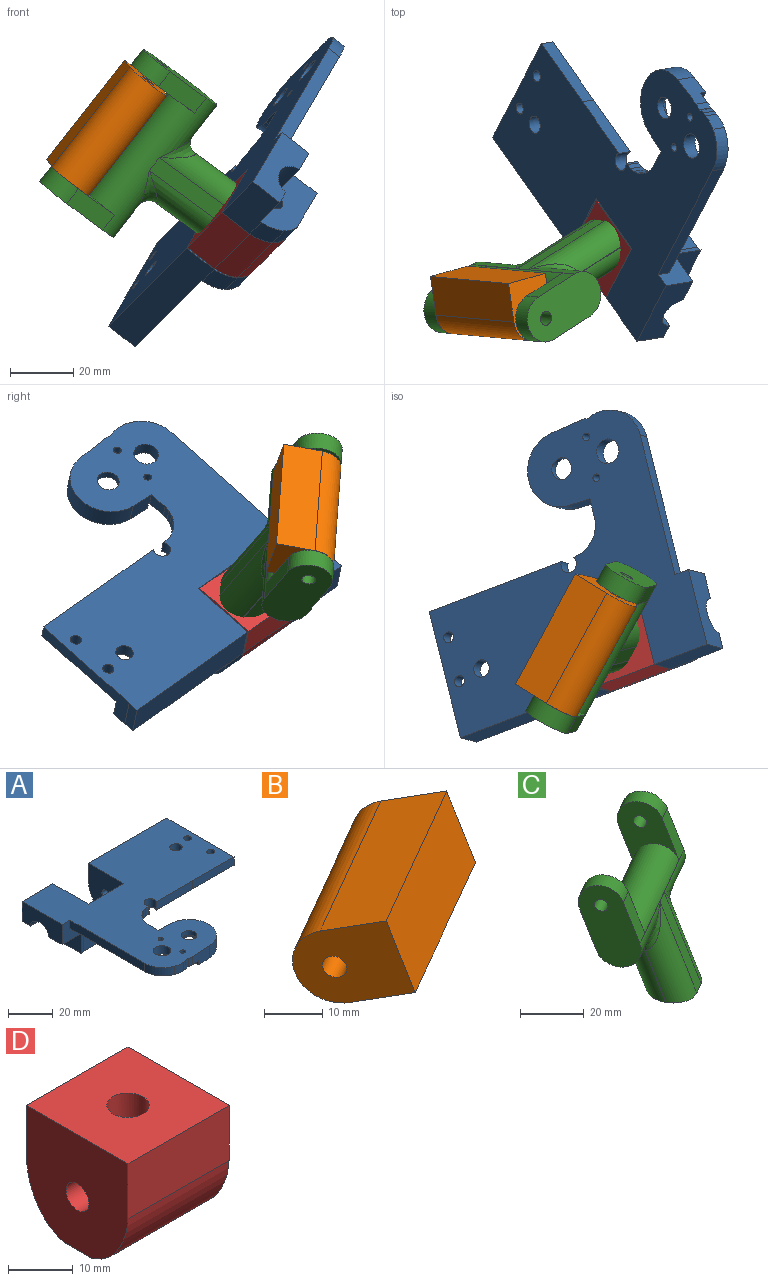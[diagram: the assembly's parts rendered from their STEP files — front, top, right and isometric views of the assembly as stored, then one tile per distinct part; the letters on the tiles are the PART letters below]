
ASSEMBLY  parts=4 mates=2
PART A: 74 faces, bbox 91.3x84.2x21.9 mm
  f0: plane 25.22x10.8mm, normal (-1,0,0), area 227.8mm2, adj f1,f2,f5,f21,f43,f72
  f1: plane 12.09x8.3mm, normal (0,0,-1), area 100.4mm2, adj f0,f7,f21,f72
  f2: plane 91.18x84.09mm, normal (0,0,1), area 4447.4mm2, adj f0,f30,f31,f32,f34,f35,f40,f41
  f3: cylinder r=2.5mm len=7.4mm, axis (1,0,0), area 116.2mm2, adj f8,f40
  f4: cylinder r=2.5mm len=7.4mm, axis (1,0,0), area 116.2mm2, adj f7,f42
  f5: plane 12.09x5.08mm, normal (0,0,-1), area 61.5mm2, adj f0,f7,f21,f43
  f6: plane 41.89x24.6mm, normal (0,0,-1), area 640.6mm2, adj f8,f9,f10,f11,f12,f13,f15,f24
  f7: plane 25.22x16mm, normal (-1,0,0), area 278.4mm2, adj f1,f4,f5,f14,f16,f19,f20,f21
  f8: plane 24.6x14mm, normal (1,0,0), area 244.2mm2, adj f3,f6,f13,f16,f17,f18,f29,f62
  f9: plane 10.48x6.3mm, normal (0,-1,0), area 66mm2, adj f6,f10,f15,f22
  f10: cylinder r=1.92mm len=6.3mm, axis (0,0,-1), area 12.4mm2, adj f6,f9,f11,f22
  f11: plane 10.52x6.64mm, normal (0.85,-0.53,0), area 78.4mm2, adj f6,f10,f12,f22
  f12: cylinder r=9.77mm len=8.3mm, axis (0,0,-1), area 62.3mm2, adj f6,f11,f13,f22
  f13: plane 47.39x17.3mm, normal (0,-1,0), area 687.6mm2, adj f6,f8,f12,f14,f16,f22
  f14: cylinder r=11.65mm len=17.3mm, axis (0,0,-1), area 33.5mm2, adj f7,f13,f16,f22,f72
  f15: plane 6.3x2.78mm, normal (0,-1,0), area 17.5mm2, adj f6,f9,f22,f61
  f16: plane 37.2x17.31mm, normal (0,0,-1), area 301.2mm2, adj f7,f8,f13,f14,f17,f20,f40,f41
  f17: cylinder r=10.47mm len=7.4mm, axis (-1,0,0), area 41.3mm2, adj f8,f16,f18,f40
  f18: cylinder r=13.47mm len=7.71mm, axis (-1,0,0), area 63mm2, adj f8,f17,f40,f62
  f19: cylinder r=13.47mm len=7.71mm, axis (-1,0,0), area 63mm2, adj f7,f20,f42,f43
  f20: cylinder r=10.47mm len=7.4mm, axis (-1,0,0), area 41.3mm2, adj f7,f16,f19,f42
  f21: cylinder r=6mm len=12.09mm, axis (-1,0,0), area 203.6mm2, adj f0,f1,f5,f7
  f22: plane 86.18x75.47mm, normal (0,0,-1), area 2643.1mm2, adj f9,f10,f11,f12,f13,f14,f15,f30
  f23: plane 8.77x4.2mm, normal (0,0.5,-0.87), area 41.3mm2, adj f24,f26,f28,f29
  f24: plane 8.78x1.57mm, normal (0,1,0), area 11.9mm2, adj f6,f23,f28,f29
  f25: plane 8.77x1.57mm, normal (0,-1,0), area 11.9mm2, adj f6,f26,f28,f29
  f26: plane 8.77x4.21mm, normal (0,-0.5,-0.87), area 41.3mm2, adj f23,f25,f28,f29
  f27: plane 7.75x3mm, normal (-1,0,0), area 17.2mm2, adj f6,f28
  f28: cone r=4mm half-angle=60deg, axis (-1,0,0), area 5.8mm2, adj f6,f23,f24,f25,f26,f27
  f29: cone r=4mm half-angle=60deg, axis (1,0,0), area 5.8mm2, adj f6,f8,f23,f24,f25,f26
  f30: plane 7.82x6.7mm, normal (0.05,1,0), area 51.4mm2, adj f2,f22,f34,f37,f39,f47
  f31: cylinder r=5.75mm len=4.5mm, axis (0,0,1), area 9.8mm2, adj f2,f22,f32,f46
  f32: plane 11.46x6.7mm, normal (0.05,-1,0), area 67.4mm2, adj f2,f22,f31,f34,f38,f39
  f33: cylinder r=8.15mm len=16.3mm, axis (0,0,1), area 191.9mm2, adj f22,f36,f37,f38,f39
  f34: cylinder r=12.15mm len=24.26mm, axis (0,0,1), area 246mm2, adj f2,f30,f32,f39
  f35: cylinder r=3.5mm len=7mm, axis (0,0,-1), area 55mm2, adj f2,f36
  f36: plane 16.3x16.3mm, normal (0,0,-1), area 170.2mm2, adj f33,f35
  f37: plane 7.61x2.2mm, normal (-1,0,0), area 16.8mm2, adj f22,f30,f33,f39
  f38: plane 7.62x2.2mm, normal (-1,0,0), area 16.8mm2, adj f22,f32,f33,f39
  f39: plane 25.04x18.66mm, normal (0,0,-1), area 194.9mm2, adj f30,f32,f33,f34,f37,f38
  f40: plane 22.2x21.8mm, normal (-1,0,0), area 440.3mm2, adj f2,f3,f16,f17,f18,f41,f62
  f41: plane 22.4x21.8mm, normal (0,1,0), area 488.3mm2, adj f2,f16,f40,f42
  f42: plane 22.2x21.8mm, normal (1,0,0), area 440.3mm2, adj f2,f4,f16,f19,f20,f41,f43
  f43: plane 19.49x11.13mm, normal (0,1,0), area 212.9mm2, adj f0,f2,f5,f7,f19,f42
  f44: plane 4.5x1.47mm, normal (0.1,-1,0), area 6.6mm2, adj f2,f22,f45,f69
  f45: plane 4.5x1.73mm, normal (0.27,-0.96,0), area 8.1mm2, adj f2,f22,f44,f46
  f46: plane 4.5x0.31mm, normal (0.44,-0.9,0), area 1.6mm2, adj f2,f22,f31,f45
  f47: plane 6.19x4.5mm, normal (1,0,0), area 27.9mm2, adj f2,f22,f30,f48
  f48: plane 4.5x1.9mm, normal (0.99,-0.11,0), area 8.6mm2, adj f2,f22,f47,f49
  f49: plane 4.5x1.83mm, normal (0.96,-0.29,0), area 8.6mm2, adj f2,f22,f48,f50
  f50: plane 4.5x1.69mm, normal (0.88,-0.47,0), area 8.6mm2, adj f2,f22,f49,f51
  f51: plane 4.5x1.49mm, normal (0.77,-0.64,0), area 8.7mm2, adj f2,f22,f50,f52
  f52: plane 4.5x1.45mm, normal (0.65,-0.76,0), area 8.6mm2, adj f2,f22,f51,f53
  f53: plane 4.5x1.7mm, normal (0.47,-0.88,0), area 8.6mm2, adj f2,f22,f52,f54
  f54: plane 4.5x1.87mm, normal (0.28,-0.96,0), area 8.8mm2, adj f2,f22,f53,f55
  f55: plane 4.5x1.9mm, normal (0.09,-1,0), area 8.6mm2, adj f2,f22,f54,f56
  f56: plane 4.5x0.65mm, normal (0,-1,0), area 2.9mm2, adj f2,f22,f55,f57
  f57: cylinder r=2.75mm len=5.5mm, axis (0,0,-1), area 54.7mm2, adj f2,f22,f56,f58
  f58: plane 23.03x4.5mm, normal (0,-1,0), area 103.6mm2, adj f2,f22,f57,f59
  f59: plane 25.95x4.5mm, normal (0,-1,0), area 116.8mm2, adj f2,f22,f58,f61
  f60: cylinder r=2.75mm len=5.5mm, axis (0,0,-1), area 77.8mm2, adj f2,f22
  f61: plane 38.82x10.8mm, normal (1,0,0), area 206.2mm2, adj f2,f6,f15,f22,f59,f63
  f62: plane 49.28x11.13mm, normal (0,1,0), area 534.7mm2, adj f2,f6,f8,f18,f40,f63
  f63: plane 10.8x3.61mm, normal (1,0,0), area 39mm2, adj f2,f6,f61,f62
  f64: cylinder r=1.22mm len=4.5mm, axis (0,0,-1), area 34.6mm2, adj f2,f22
  f65: cylinder r=1.22mm len=4.5mm, axis (0,0,-1), area 34.4mm2, adj f2,f22
  f66: cylinder r=3.92mm len=7.84mm, axis (0,0,-1), area 110.9mm2, adj f2,f22
  f67: cylinder r=1.75mm len=4.5mm, axis (0,0,-1), area 49.5mm2, adj f2,f22
  f68: cylinder r=1.75mm len=4.5mm, axis (0,0,-1), area 49.5mm2, adj f2,f22
  f69: plane 4.5x0.02mm, normal (-1,0,0), area 0.1mm2, adj f2,f22,f44,f71
  f70: cylinder r=11.73mm len=11.04mm, axis (0,0,-1), area 64.5mm2, adj f2,f22,f71,f73
  f71: cylinder r=11.89mm len=5.18mm, axis (0,0,-1), area 23.8mm2, adj f2,f22,f69,f70
  f72: plane 12.09x10.8mm, normal (0,-1,0), area 98.7mm2, adj f0,f1,f2,f14,f22,f73
  f73: plane 47.01x4.5mm, normal (-1,0,0), area 211.6mm2, adj f2,f22,f70,f72
PART B: 7 faces, bbox 45.5x38.9x18.8 mm
  f0: plane 18.89x18.82mm, normal (0.87,0.5,0), area 260.7mm2, adj f1,f3,f4,f5,f6
  f1: plane 40.51x30.17mm, normal (0.17,-0.3,-0.94), area 500mm2, adj f0,f2,f4,f6
  f2: plane 18.89x18.82mm, normal (-0.87,-0.5,0), area 260.7mm2, adj f1,f3,f4,f5,f6
  f3: plane 40.51x30.17mm, normal (-0.17,0.3,0.94), area 500mm2, adj f0,f2,f4,f6
  f4: plane 37.21x24.44mm, normal (0.47,-0.81,0.34), area 600mm2, adj f0,f1,f2,f3
  f5: cylinder r=2.2mm len=36.84mm, axis (0.87,0.5,0), area 552.9mm2, adj f0,f2
  f6: cylinder r=7.5mm len=39.67mm, axis (0.87,0.5,0), area 942.5mm2, adj f0,f1,f2,f3
PART C: 32 faces, bbox 56.1x44.2x55.5 mm
  f0: plane 19.65x18.3mm, normal (0,0,-1), area 152.3mm2, adj f14,f15,f16,f17,f18,f19,f20,f21
  f1: plane 25.1x17.33mm, normal (-0.87,-0.5,0), area 224.8mm2, adj f2,f3,f4,f5,f7
  f2: plane 48.61x31.2mm, normal (0.47,-0.81,0.34), area 192.3mm2, adj f1,f3,f5,f6,f9,f10,f11
  f3: cylinder r=7.5mm len=53.4mm, axis (-0.87,-0.5,0), area 1716.9mm2, adj f1,f2,f4,f6,f8,f10,f11,f13
  f4: plane 14.88x7.9mm, normal (-0.47,0.81,-0.34), area 95mm2, adj f1,f3,f5,f6
  f5: cylinder r=7.5mm len=15.65mm, axis (-0.87,-0.5,0), area 143.3mm2, adj f1,f2,f4,f6
  f6: plane 30.03x17.73mm, normal (0.87,0.5,0), area 401.4mm2, adj f2,f3,f4,f5,f7
  f7: cylinder r=2.2mm len=7.4mm, axis (-0.87,-0.5,0), area 82.9mm2, adj f1,f6
  f8: plane 14.88x7.9mm, normal (-0.47,0.81,-0.34), area 95mm2, adj f3,f9,f10,f11
  f9: cylinder r=7.5mm len=15.65mm, axis (0.87,0.5,0), area 143.3mm2, adj f2,f8,f10,f11
  f10: plane 30.03x17.73mm, normal (-0.87,-0.5,0), area 401.4mm2, adj f2,f3,f8,f9,f12
  f11: plane 25.1x17.33mm, normal (0.87,0.5,0), area 224.8mm2, adj f2,f3,f8,f9,f12
  f12: cylinder r=2.2mm len=7.4mm, axis (0.87,0.5,0), area 82.9mm2, adj f10,f11
  f13: cylinder r=7.54mm len=5.09mm, axis (0.87,0.5,0), area 0.2mm2, adj f3,f15,f19,f21,f22,f25
  f14: plane 27.82x11.37mm, normal (-0.47,0.81,-0.34), area 154mm2, adj f0,f3,f18,f20
  f15: plane 32.92x12.97mm, normal (0.47,-0.81,0.34), area 182.1mm2, adj f0,f13,f19,f21
  f16: plane 18.68x6.05mm, normal (-0.87,-0.5,0), area 3.9mm2, adj f0,f20,f21,f23
  f17: plane 18.68x6.05mm, normal (0.87,0.5,0), area 3.9mm2, adj f0,f18,f19,f26
  f18: cylinder r=7.4mm len=32.89mm, axis (0.17,-0.3,-0.94), area 263.3mm2, adj f0,f14,f17,f27
  f19: cylinder r=7.4mm len=35.45mm, axis (-0.17,0.3,0.94), area 304.1mm2, adj f0,f13,f15,f17,f25
  f20: cylinder r=7.4mm len=32.89mm, axis (-0.17,0.3,0.94), area 263.3mm2, adj f0,f14,f16,f24
  f21: cylinder r=7.4mm len=35.45mm, axis (0.17,-0.3,-0.94), area 304.1mm2, adj f0,f13,f15,f16,f22
  f22: bspline ~14.42x13.02mm, area 68.2mm2, adj f3,f13,f21,f23
  f23: torus R=12.5mm, axis (-0.87,-0.5,0), area 1.2mm2, adj f3,f16,f22,f24
  f24: bspline ~15.43x9.48mm, area 68.2mm2, adj f3,f20,f23
  f25: bspline ~14.42x10.41mm, area 68.2mm2, adj f3,f13,f19,f26
  f26: torus R=12.5mm, axis (-0.87,-0.5,0), area 1.2mm2, adj f3,f17,f25,f27
  f27: bspline ~15.96x9.48mm, area 68.2mm2, adj f3,f18,f26
  f28: cylinder r=6.1mm len=12.2mm, axis (0,0,-1), area 46mm2, adj f0,f29
  f29: plane 12.2x12.2mm, normal (0,0,-1), area 58.8mm2, adj f28,f31
  f30: plane 8.6x8.6mm, normal (0,0,-1), area 58.1mm2, adj f31
  f31: cylinder r=4.3mm len=11.3mm, axis (0,0,-1), area 305.3mm2, adj f29,f30
PART D: 14 faces, bbox 22x22x21.8 mm
  f0: cylinder r=3.25mm len=21.8mm, axis (0,0,-1), area 401.8mm2, adj f2,f4,f7,f10,f11,f12,f13
  f1: plane 22x21.8mm, normal (-1,0,0), area 411.4mm2, adj f4,f5,f6,f7,f8,f9,f10,f12
  f2: plane 9.98x6.17mm, normal (0,0,-1), area 51.5mm2, adj f0,f3,f7,f10
  f3: plane 22x21.8mm, normal (1,0,0), area 411.4mm2, adj f2,f5,f6,f7,f8,f9,f10,f11
  f4: plane 9.98x6.17mm, normal (0,0,-1), area 51.5mm2, adj f0,f1,f7,f10
  f5: plane 22x10.37mm, normal (0,-1,0), area 228.1mm2, adj f1,f3,f8,f13
  f6: plane 22x11.13mm, normal (0,1,0), area 244.9mm2, adj f1,f3,f9,f13
  f7: cylinder r=10.47mm len=22mm, axis (-1,0,0), area 122.6mm2, adj f0,f1,f2,f3,f4,f8
  f8: cylinder r=14.61mm len=22mm, axis (-1,0,0), area 203.1mm2, adj f1,f3,f5,f7
  f9: cylinder r=13.47mm len=22mm, axis (-1,0,0), area 187.2mm2, adj f1,f3,f6,f10
  f10: cylinder r=10.47mm len=22mm, axis (-1,0,0), area 122.6mm2, adj f0,f1,f2,f3,f4,f9
  f11: cylinder r=2.5mm len=8.92mm, axis (1,0,0), area 130.5mm2, adj f0,f3
  f12: cylinder r=2.5mm len=8.92mm, axis (1,0,0), area 130.4mm2, adj f0,f1
  f13: plane 22x22mm, normal (0,0,1), area 450.8mm2, adj f0,f1,f3,f5,f6
PLACE A rot(axis=(-0.41,-0.24,0.88),142.6deg) t=(11.51,-104.42,-42.89)mm
PLACE B rot(axis=(-0.45,-0.07,0.89),146.9deg) t=(15.12,-117.5,-59.5)mm
PLACE C rot(axis=(-0.42,-0.19,0.89),153.4deg) t=(5.31,-104.97,-50.26)mm
PLACE D rot(axis=(-0.41,-0.24,0.88),142.6deg) t=(11.61,-104.56,-42.79)mm
MATE revolute B.f5 <-> C.f12  axis (-0.62,0.06,-0.79) through (-42.85,-161.35,-44.39)mm
MATE revolute D.f11 <-> A.f3  axis (-0.5,0.71,-0.5) through (18.34,-148.31,-54.82)mm
